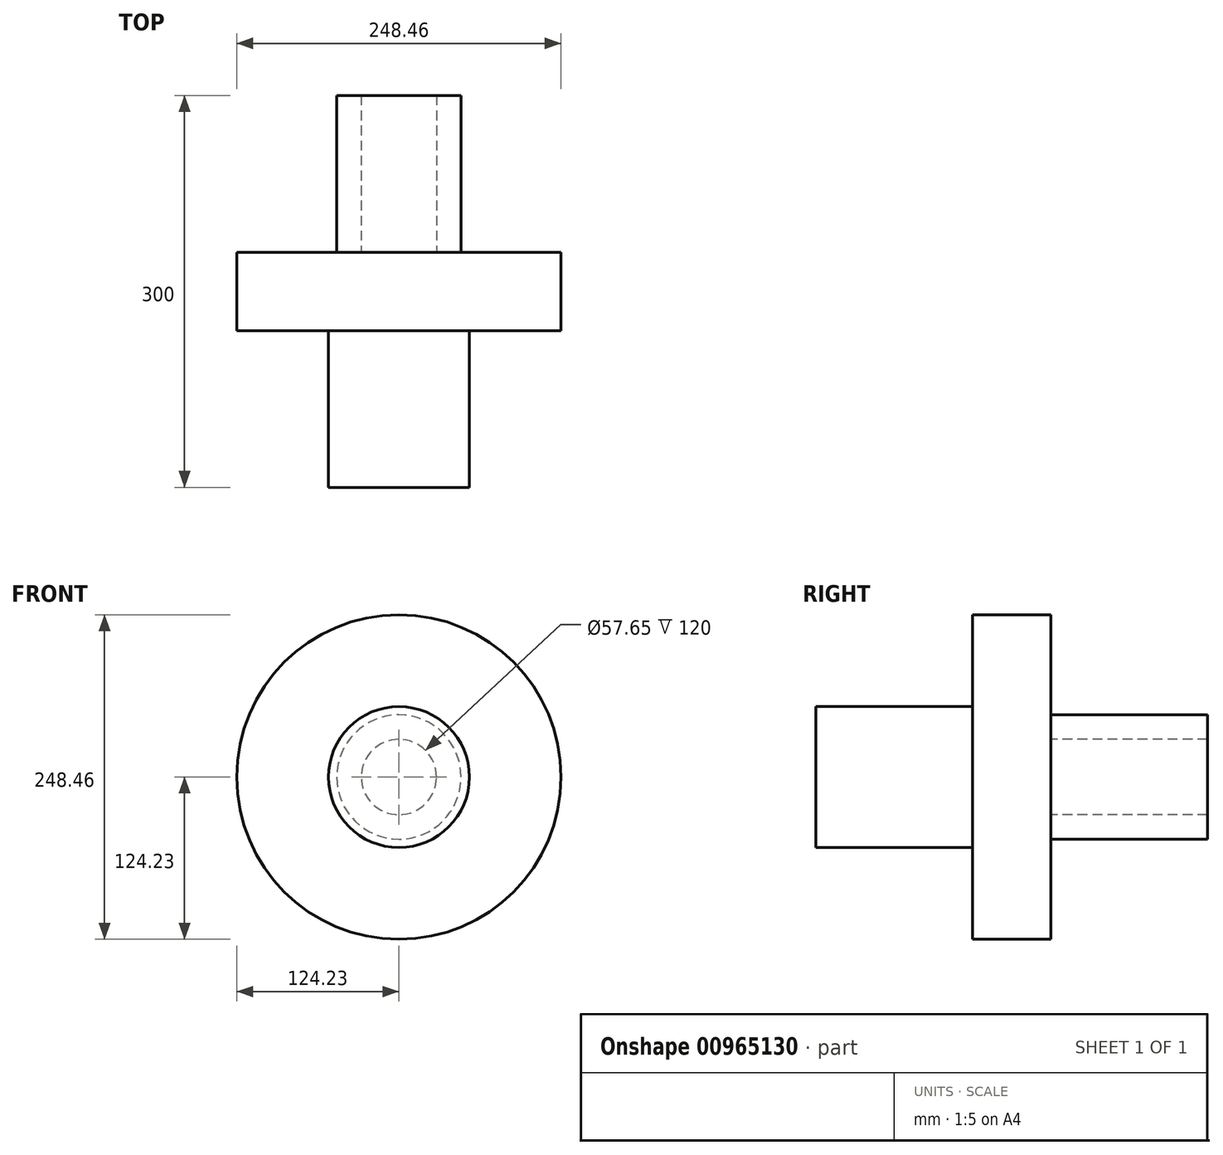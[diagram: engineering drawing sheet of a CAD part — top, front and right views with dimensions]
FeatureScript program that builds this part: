
annotation { "Feature Type Name" : "Feature", "Feature Type Description" : "" }
export const myFeature = defineFeature(function(context is Context, id is Id, definition is map)
    precondition{}
    {
        {
            var Q0;
            Q0=qCreatedBy(makeId("Front.planeOp"),FACE);
            var sketch = newSketch(context, id + "F0", { "sketchPlane" : qUnion([Q0])});
            skCircle(sketch, "E0", {"center": v(0, 0) * mm, "radius": 47.6 * mm});
            skSolve(sketch);
        }
        {
            var Q0;
            Q0=makeQuery(id+"F0.imprint","IMPRINT",FACE,{"disambiguationData":[TD([[makeQuery(id+"F0.imprint","IMPRINT",EDGE,{"derivedFrom":sQuery(id+"F0.wireOp",EDGE,"E0")}),1.0]])]});
            extrude(context, id + "F1", {"entities" : qUnion([Q0]), "depth" : 120 * mm, "offsetDistance" : 25.4 * mm});
        }
        {
            var Q0;
            Q0=makeQuery(id+"F1.opExtrude","CAP_FACE",FACE,{"disambiguationData":[OSD([sQuery(id+"F0.wireOp",EDGE,"E0")])],"isStart":false});
            var sketch = newSketch(context, id + "F2", { "sketchPlane" : qUnion([Q0])});
            skCircle(sketch, "E1", {"center": v(0, 0) * mm, "radius": 28.83 * mm});
            skSolve(sketch);
        }
        {
            var Q0;
            Q0=makeQuery(id+"F2.imprint","IMPRINT",FACE,{"disambiguationData":[TD([[makeQuery(id+"F2.imprint","IMPRINT",EDGE,{"derivedFrom":sQuery(id+"F2.wireOp",EDGE,"E1")}),1.0]])]});
            extrude(context, id + "F3", {"entities" : qUnion([Q0]), "operationType" : NewBodyOperationType.REMOVE, "endBound" : BoundingType.THROUGH_ALL, "oppositeDirection" : true, "depth" : 25.4 * mm, "offsetDistance" : 25.4 * mm});
        }
        {
            var Q0;
            Q0 = qSketchRegion(id + "F2", true);
            var sketch = newSketch(context, id + "F4", { "sketchPlane" : qUnion([Q0])});
            skCircle(sketch, "E2", {"center": v(0, 0) * mm, "radius": 124.23 * mm});
            skSolve(sketch);
        }
        {
            var Q0;
            Q0=makeQuery(id+"F2.imprint","IMPRINT",FACE,{"disambiguationData":[TD([[makeQuery(id+"F2.imprint","IMPRINT",EDGE,{"derivedFrom":sQuery(id+"F2.wireOp",EDGE,"E1")}),1.0]])]});
            var Q1;
            Q1=makeQuery(id+"F4.imprint","IMPRINT",FACE,{"disambiguationData":[TD([[makeQuery(id+"F4.imprint","IMPRINT",EDGE,{"derivedFrom":sQuery(id+"F4.wireOp",EDGE,"E2")}),1.0]])]});
            extrude(context, id + "F5", {"entities" : qUnion([Q0, Q1]), "operationType" : NewBodyOperationType.ADD, "depth" : 60 * mm, "offsetDistance" : 25.4 * mm});
        }
        {
            var Q0;
            {var subQ0=sQuery(id+"F2.wireOp",EDGE,"E1");Q0=makeQuery(id+"F5.boolean.opBoolean","MERGE",FACE,{"derivedFrom":[makeQuery(id+"F5.opExtrude","CAP_FACE",FACE,{"disambiguationData":[OSD([subQ0])],"isStart":false}),makeQuery(id+"F5.opExtrude","CAP_FACE",FACE,{"disambiguationData":[OSD([subQ0,sQuery(id+"F4.wireOp",EDGE,"E2")])],"isStart":false})]});}
            var sketch = newSketch(context, id + "F6", { "sketchPlane" : qUnion([Q0])});
            skSolve(sketch);
        }
        {
            var Q0;
            Q0=makeQuery(id+"F6.imprint","IMPRINT",FACE,{"disambiguationData":[TD([[makeQuery(id+"F6.imprint","IMPRINT",EDGE,{"derivedFrom":makeQuery(id+"F5.opExtrude","CAP_EDGE",EDGE,{"disambiguationData":[OSD([sQuery(id+"F4.wireOp",EDGE,"E2")])],"isStart":false})}),1.0]])]});
            var sketch = newSketch(context, id + "F7", { "sketchPlane" : qUnion([Q0])});
            skPoint(sketch, "E3", {"position": v(0, 0) * mm});
            skSolve(sketch);
        }
        {
            var Q0;
            Q0=makeQuery(id+"F7.imprint","IMPRINT",FACE,{"disambiguationData":[TD([[makeQuery(id+"F7.imprint","IMPRINT",EDGE,{"derivedFrom":makeQuery(id+"F6.imprint","IMPRINT",EDGE,{"derivedFrom":makeQuery(id+"F5.opExtrude","CAP_EDGE",EDGE,{"disambiguationData":[OSD([sQuery(id+"F4.wireOp",EDGE,"E2")])],"isStart":false})})}),1.0]])]});
            var sketch = newSketch(context, id + "F8", { "sketchPlane" : qUnion([Q0])});
            skPoint(sketch, "E4", {"position": v(0, 0) * mm});
            skCircle(sketch, "E5", {"center": v(0, 0) * mm, "radius": 53.99 * mm});
            skSolve(sketch);
        }
        {
            var Q0;
            Q0 = qSketchRegion(id + "F8", true);
            extrude(context, id + "F9", {"entities" : qUnion([Q0]), "operationType" : NewBodyOperationType.ADD, "depth" : 120 * mm, "offsetDistance" : 25 * mm});
        }
    });
